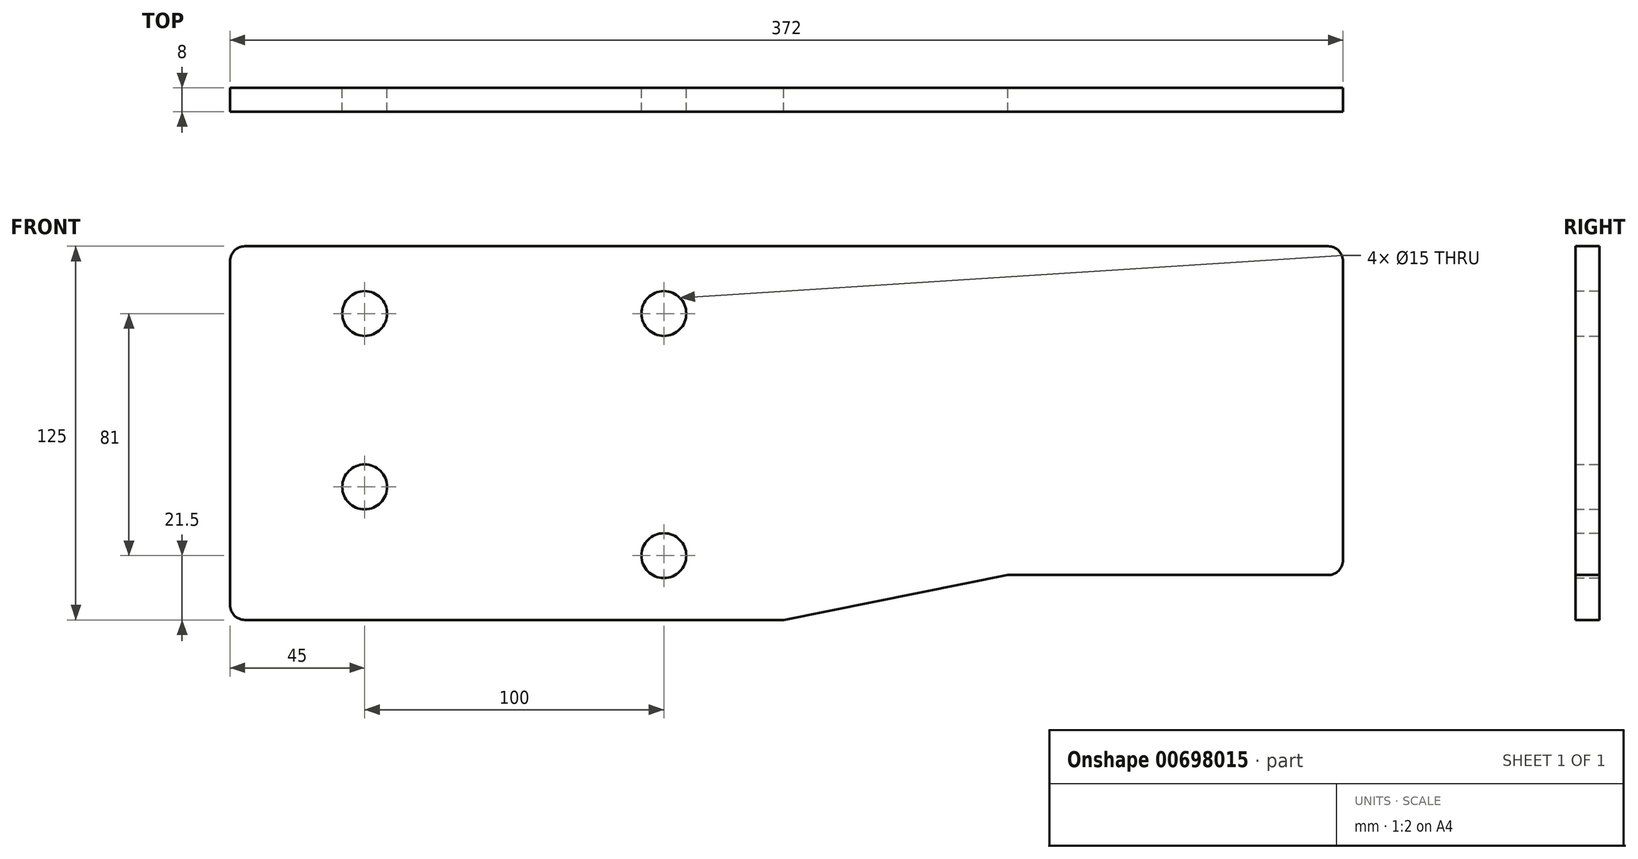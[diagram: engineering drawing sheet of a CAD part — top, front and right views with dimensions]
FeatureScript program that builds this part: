
annotation { "Feature Type Name" : "Feature", "Feature Type Description" : "" }
export const myFeature = defineFeature(function(context is Context, id is Id, definition is map)
    precondition{}
    {
        {
            var Q0;
            Q0=qCreatedBy(makeId("Front.planeOp"),FACE);
            var sketch = newSketch(context, id + "F0", { "sketchPlane" : qUnion([Q0])});
            skLineSegment(sketch, "E0", {"start": v(0, 5) * mm, "end": v(0, 120) * mm});
            skLineSegment(sketch, "E1", {"start": v(5, 125) * mm, "end": v(367, 125) * mm});
            skLineSegment(sketch, "E2", {"start": v(372, 120) * mm, "end": v(372, 20) * mm});
            skLineSegment(sketch, "E3", {"start": v(367, 15) * mm, "end": v(260, 15) * mm});
            skLineSegment(sketch, "E4", {"start": v(260, 15) * mm, "end": v(185, 0) * mm});
            skLineSegment(sketch, "E5", {"start": v(185, 0) * mm, "end": v(5, 0) * mm});
            skCircle(sketch, "E6", {"center": v(45, 102.5) * mm, "radius": 7.5 * mm});
            skCircle(sketch, "E7", {"center": v(145, 102.5) * mm, "radius": 7.5 * mm});
            skCircle(sketch, "E8", {"center": v(145, 21.5) * mm, "radius": 7.5 * mm});
            skCircle(sketch, "E9", {"center": v(45, 44.5) * mm, "radius": 7.5 * mm});
            skPoint(sketch, "E10.visualSharp", {"position": v(372, 125) * mm});
            skArc(sketch, "E10.filletArc", {"start": v(372, 120) * mm, "mid": v(370.54, 123.54) * mm, "end": v(367, 125) * mm});
            skPoint(sketch, "E11.visualSharp", {"position": v(372, 15) * mm});
            skArc(sketch, "E11.filletArc", {"start": v(367, 15) * mm, "mid": v(370.54, 16.46) * mm, "end": v(372, 20) * mm});
            skPoint(sketch, "E12.visualSharp", {"position": v(0, 0) * mm});
            skArc(sketch, "E12.filletArc", {"start": v(0, 5) * mm, "mid": v(1.46, 1.46) * mm, "end": v(5, 0) * mm});
            skPoint(sketch, "E13.visualSharp", {"position": v(0, 125) * mm});
            skArc(sketch, "E13.filletArc", {"start": v(5, 125) * mm, "mid": v(1.46, 123.54) * mm, "end": v(0, 120) * mm});
            skSolve(sketch);
        }
        {
            var Q0;
            Q0=makeQuery(id+"F0.imprint","IMPRINT",FACE,{"disambiguationData":[TD([[makeQuery(id+"F0.imprint","IMPRINT",EDGE,{"derivedFrom":sQuery(id+"F0.wireOp",EDGE,"E0")}),-1.0]])]});
            extrude(context, id + "F1", {"entities" : qUnion([Q0]), "depth" : 8 * mm, "offsetDistance" : 25 * mm});
        }
    });
